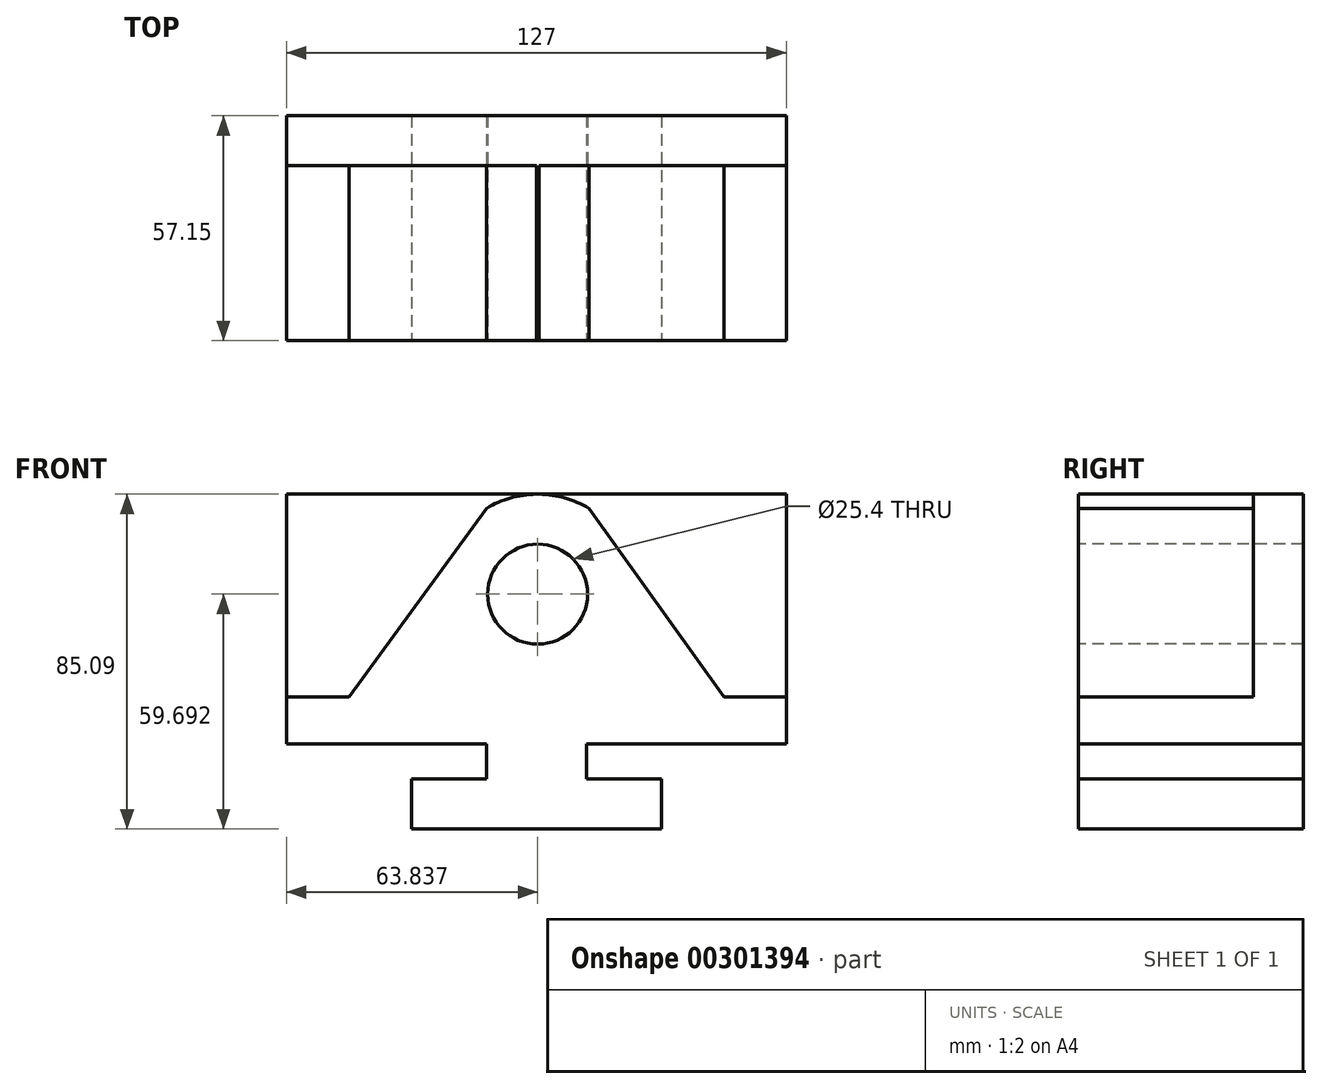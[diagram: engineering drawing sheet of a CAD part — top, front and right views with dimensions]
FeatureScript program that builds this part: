
annotation { "Feature Type Name" : "Feature", "Feature Type Description" : "" }
export const myFeature = defineFeature(function(context is Context, id is Id, definition is map)
    precondition{}
    {
        {
            var Q0;
            Q0=qCreatedBy(makeId("Top.planeOp"),FACE);
            var sketch = newSketch(context, id + "F0", { "sketchPlane" : qUnion([Q0])});
            skLineSegment(sketch, "E0.bottom", {"start": v(0, 0) * mm, "end": v(127, 0) * mm});
            skLineSegment(sketch, "E0.top", {"start": v(0, 57.15) * mm, "end": v(127, 57.15) * mm});
            skLineSegment(sketch, "E0.left", {"start": v(0, 0) * mm, "end": v(0, 57.15) * mm});
            skLineSegment(sketch, "E0.right", {"start": v(127, 0) * mm, "end": v(127, 57.15) * mm});
            skLineSegment(sketch, "E1", {"start": v(0, 44.45) * mm, "end": v(127, 44.45) * mm});
            skLineSegment(sketch, "E2", {"start": v(15.88, 44.45) * mm, "end": v(15.88, 0) * mm});
            skLineSegment(sketch, "E3", {"start": v(111.12, 0) * mm, "end": v(111.12, 44.45) * mm});
            skSolve(sketch);
        }
        {
            var Q0;
            Q0 = qSketchRegion(id + "F0", true);
            extrude(context, id + "F1", {"entities" : qUnion([Q0]), "depth" : 85.1 * mm});
        }
        {
            var Q0;
            Q0=makeQuery(id+"F1.opExtrude","SWEPT_FACE",FACE,{"disambiguationData":[OSD([sQuery(id+"F0.wireOp",EDGE,"E0.bottom")])]});
            var sketch = newSketch(context, id + "F2", { "sketchPlane" : qUnion([Q0])});
            skLineSegment(sketch, "E4", {"start": v(0, 85.1) * mm, "end": v(127, 85.1) * mm});
            skLineSegment(sketch, "E5", {"start": v(127, 85.1) * mm, "end": v(127, 21.59) * mm});
            skLineSegment(sketch, "E6", {"start": v(127, 21.59) * mm, "end": v(76.2, 21.59) * mm});
            skLineSegment(sketch, "E7", {"start": v(76.2, 21.59) * mm, "end": v(76.2, 12.7) * mm});
            skLineSegment(sketch, "E8", {"start": v(76.2, 12.7) * mm, "end": v(95.25, 12.7) * mm});
            skLineSegment(sketch, "E9", {"start": v(95.25, 12.7) * mm, "end": v(95.25, 0) * mm});
            skLineSegment(sketch, "E10", {"start": v(31.75, 0) * mm, "end": v(31.75, 12.7) * mm});
            skLineSegment(sketch, "E11", {"start": v(31.75, 12.7) * mm, "end": v(50.8, 12.7) * mm});
            skLineSegment(sketch, "E12", {"start": v(50.8, 12.7) * mm, "end": v(50.8, 21.59) * mm});
            skLineSegment(sketch, "E13", {"start": v(50.8, 21.59) * mm, "end": v(0, 21.59) * mm});
            skLineSegment(sketch, "E14", {"start": v(0, 21.59) * mm, "end": v(0, 85.1) * mm});
            skLineSegment(sketch, "E15", {"start": v(31.75, 0) * mm, "end": v(95.25, 0) * mm});
            skLineSegment(sketch, "E16", {"start": v(127, 21.59) * mm, "end": v(127, 33.54) * mm});
            skLineSegment(sketch, "E17", {"start": v(127, 33.54) * mm, "end": v(111.12, 33.54) * mm});
            skLineSegment(sketch, "E18", {"start": v(111.12, 33.54) * mm, "end": v(76.82, 81.52) * mm});
            skLineSegment(sketch, "E19", {"start": v(50.85, 81.52) * mm, "end": v(15.87, 33.54) * mm});
            skLineSegment(sketch, "E20", {"start": v(15.88, 33.54) * mm, "end": v(0, 33.54) * mm});
            skLineSegment(sketch, "E21", {"start": v(0, 33.54) * mm, "end": v(0, 21.59) * mm});
            skLineSegment(sketch, "E22", {"start": v(63.5, 85.1) * mm, "end": v(63.5, 0) * mm, "construction": true});
            skArc(sketch, "E23", {"start": v(76.82, 81.52) * mm, "mid": v(63.84, 85.1) * mm, "end": v(50.85, 81.52) * mm});
            skCircle(sketch, "E24", {"center": v(63.84, 59.7) * mm, "radius": 12.7 * mm});
            skSolve(sketch);
        }
        {
            var Q0;
            {var subQ1=sQuery(id+"F2.wireOp",EDGE,"E14");Q0=makeQuery(id+"F2.imprint","IMPRINT",FACE,{"disambiguationData":[TD([[makeQuery(id+"F2.imprint","IMPRINT",EDGE,{"derivedFrom":subQ1}),1.0]])]});}
            var Q1;
            {var subQ1=sQuery(id+"F2.wireOp",EDGE,"E5");Q1=makeQuery(id+"F2.imprint","IMPRINT",FACE,{"disambiguationData":[TD([[makeQuery(id+"F2.imprint","IMPRINT",EDGE,{"derivedFrom":subQ1}),-1.0]])]});}
            extrude(context, id + "F3", {"entities" : qUnion([Q0, Q1]), "operationType" : NewBodyOperationType.REMOVE, "oppositeDirection" : true, "depth" : 44.45 * mm});
        }
        {
            var Q0;
            {var subQ5=sQuery(id+"F2.wireOp",EDGE,"E6");Q0=makeQuery(id+"F2.imprint","IMPRINT",FACE,{"disambiguationData":[TD([[makeQuery(id+"F2.imprint","IMPRINT",EDGE,{"derivedFrom":subQ5}),1.0]])]});}
            var Q1;
            {var subQ1=sQuery(id+"F2.wireOp",EDGE,"E10");Q1=makeQuery(id+"F2.imprint","IMPRINT",FACE,{"disambiguationData":[TD([[makeQuery(id+"F2.imprint","IMPRINT",EDGE,{"derivedFrom":subQ1}),1.0]])]});}
            var Q2;
            Q2=makeQuery(id+"F2.imprint","IMPRINT",FACE,{"disambiguationData":[TD([[makeQuery(id+"F2.imprint","IMPRINT",EDGE,{"derivedFrom":sQuery(id+"F2.wireOp",EDGE,"E24")}),1.0]])]});
            extrude(context, id + "F4", {"entities" : qUnion([Q0, Q1, Q2]), "operationType" : NewBodyOperationType.REMOVE, "endBound" : BoundingType.THROUGH_ALL, "oppositeDirection" : true, "depth" : 25.4 * mm});
        }
    });
